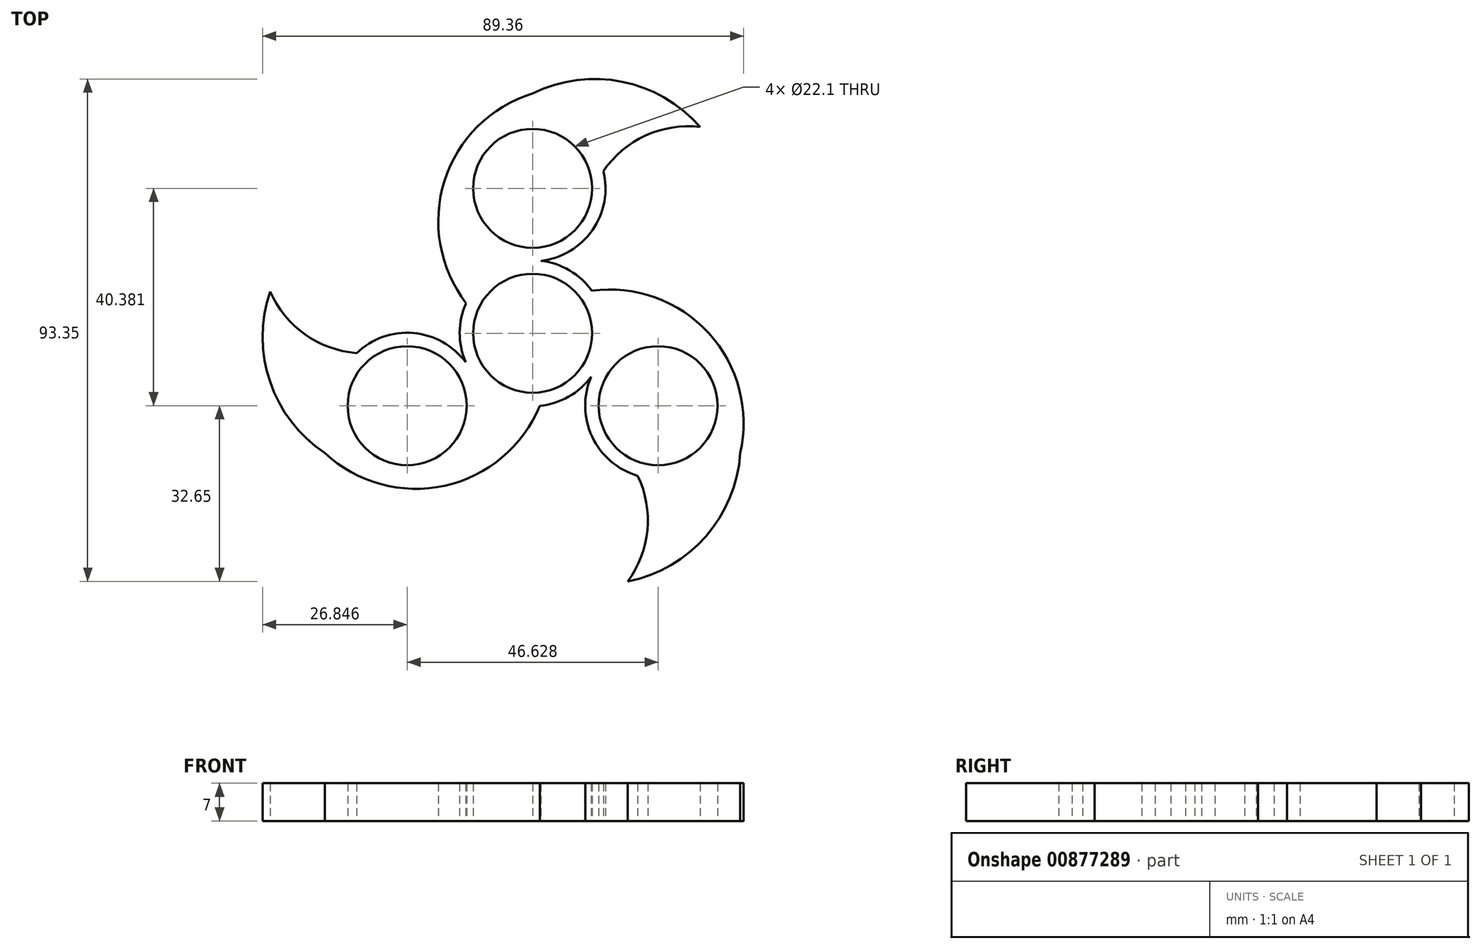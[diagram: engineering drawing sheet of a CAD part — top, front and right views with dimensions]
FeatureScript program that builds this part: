
annotation { "Feature Type Name" : "Feature", "Feature Type Description" : "" }
export const myFeature = defineFeature(function(context is Context, id is Id, definition is map)
    precondition{}
    {
        {
            var Q0;
            Q0=qCreatedBy(makeId("Top.planeOp"),FACE);
            var sketch = newSketch(context, id + "F0", { "sketchPlane" : qUnion([Q0])});
            skCircle(sketch, "E0", {"center": v(0, 0) * mm, "radius": 11.05 * mm});
            skCircle(sketch, "E1", {"center": v(0, 0) * mm, "radius": 13.55 * mm});
            skCircle(sketch, "E2", {"center": v(0, 26.92) * mm, "radius": 11.05 * mm});
            skCircle(sketch, "E3", {"center": v(0, 26.92) * mm, "radius": 13.55 * mm});
            skCircle(sketch, "E4.1.0", {"center": v(-23.31, -13.46) * mm, "radius": 11.05 * mm});
            skCircle(sketch, "E4.1.1", {"center": v(-23.31, -13.46) * mm, "radius": 13.55 * mm});
            skCircle(sketch, "E4.2.0", {"center": v(23.31, -13.46) * mm, "radius": 11.05 * mm});
            skCircle(sketch, "E4.2.1", {"center": v(23.31, -13.46) * mm, "radius": 13.55 * mm});
            skArc(sketch, "E5", {"start": v(31.1, 38.36) * mm, "mid": v(16.6, 46.74) * mm, "end": v(0, 44.54) * mm});
            skArc(sketch, "E6", {"start": v(31.1, 38.36) * mm, "mid": v(21, 36.74) * mm, "end": v(13.16, 30.14) * mm});
            skArc(sketch, "E7.1.0", {"start": v(-48.77, 7.75) * mm, "mid": v(-48.78, -9) * mm, "end": v(-38.58, -22.27) * mm});
            skArc(sketch, "E7.1.1", {"start": v(-48.77, 7.75) * mm, "mid": v(-42.3, -0.19) * mm, "end": v(-32.68, -3.67) * mm});
            skArc(sketch, "E7.2.0", {"start": v(17.67, -46.1) * mm, "mid": v(32.18, -37.75) * mm, "end": v(38.58, -22.27) * mm});
            skArc(sketch, "E7.2.1", {"start": v(17.67, -46.1) * mm, "mid": v(21.32, -36.55) * mm, "end": v(19.52, -26.47) * mm});
            skArc(sketch, "E8", {"start": v(0, 44.54) * mm, "mid": v(-16.37, 28.3) * mm, "end": v(-12.34, 5.6) * mm});
            skArc(sketch, "E9.1.0", {"start": v(-38.58, -22.27) * mm, "mid": v(-16.32, -28.33) * mm, "end": v(1.33, -13.48) * mm});
            skArc(sketch, "E9.2.0", {"start": v(38.58, -22.27) * mm, "mid": v(32.7, 0.03) * mm, "end": v(11.01, 7.9) * mm});
            skSolve(sketch);
        }
        {
            var Q0;
            {var subQ0=sQuery(id+"F0.wireOp",EDGE,"E1");var subQ1=sQuery(id+"F0.wireOp",EDGE,"E3");var subQ2=makeQuery(id+"F0.imprint","INTERSECT",VERTEX,{"disambiguationData":[OD(0.0)],"derivedFrom":[subQ1,subQ0]});Q0=makeQuery(id+"F0.imprint","IMPRINT",FACE,{"disambiguationData":[TD([[makeQuery(id+"F0.imprint","IMPRINT",EDGE,{"disambiguationData":[TD([[subQ2,1.0]])],"derivedFrom":subQ1}),1.0]])]});}
            var Q1;
            {var subQ0=sQuery(id+"F0.wireOp",EDGE,"E1");var subQ1=sQuery(id+"F0.wireOp",EDGE,"E4.1.1");var subQ2=makeQuery(id+"F0.imprint","INTERSECT",VERTEX,{"disambiguationData":[OD(0.0)],"derivedFrom":[subQ1,subQ0]});Q1=makeQuery(id+"F0.imprint","IMPRINT",FACE,{"disambiguationData":[TD([[makeQuery(id+"F0.imprint","IMPRINT",EDGE,{"disambiguationData":[TD([[subQ2,1.0]])],"derivedFrom":subQ1}),1.0]])]});}
            var Q2;
            {var subQ0=sQuery(id+"F0.wireOp",EDGE,"E1");var subQ1=sQuery(id+"F0.wireOp",EDGE,"E4.2.1");var subQ2=makeQuery(id+"F0.imprint","INTERSECT",VERTEX,{"disambiguationData":[OD(0.0)],"derivedFrom":[subQ1,subQ0]});Q2=makeQuery(id+"F0.imprint","IMPRINT",FACE,{"disambiguationData":[TD([[makeQuery(id+"F0.imprint","IMPRINT",EDGE,{"disambiguationData":[TD([[subQ2,1.0]])],"derivedFrom":subQ1}),1.0]])]});}
            var Q3;
            Q3=makeQuery(id+"F0.imprint","IMPRINT",FACE,{"disambiguationData":[TD([[makeQuery(id+"F0.imprint","IMPRINT",EDGE,{"derivedFrom":sQuery(id+"F0.wireOp",EDGE,"E2")}),-1.0]])]});
            var Q4;
            Q4=makeQuery(id+"F0.imprint","IMPRINT",FACE,{"disambiguationData":[TD([[makeQuery(id+"F0.imprint","IMPRINT",EDGE,{"derivedFrom":sQuery(id+"F0.wireOp",EDGE,"E4.1.0")}),-1.0]])]});
            var Q5;
            Q5=makeQuery(id+"F0.imprint","IMPRINT",FACE,{"disambiguationData":[TD([[makeQuery(id+"F0.imprint","IMPRINT",EDGE,{"derivedFrom":sQuery(id+"F0.wireOp",EDGE,"E4.2.0")}),-1.0]])]});
            var Q6;
            Q6=makeQuery(id+"F0.imprint","IMPRINT",FACE,{"disambiguationData":[TD([[makeQuery(id+"F0.imprint","IMPRINT",EDGE,{"derivedFrom":sQuery(id+"F0.wireOp",EDGE,"E0")}),-1.0]])]});
            var Q7;
            Q7=makeQuery(id+"F0.imprint","IMPRINT",FACE,{"disambiguationData":[TD([[makeQuery(id+"F0.imprint","IMPRINT",EDGE,{"derivedFrom":sQuery(id+"F0.wireOp",EDGE,"E7.1.0")}),1.0]])]});
            var Q8;
            Q8=makeQuery(id+"F0.imprint","IMPRINT",FACE,{"disambiguationData":[TD([[makeQuery(id+"F0.imprint","IMPRINT",EDGE,{"derivedFrom":sQuery(id+"F0.wireOp",EDGE,"E5")}),1.0]])]});
            var Q9;
            Q9=makeQuery(id+"F0.imprint","IMPRINT",FACE,{"disambiguationData":[TD([[makeQuery(id+"F0.imprint","IMPRINT",EDGE,{"derivedFrom":sQuery(id+"F0.wireOp",EDGE,"E7.2.0")}),1.0]])]});
            extrude(context, id + "F1", {"entities" : qUnion([Q0, Q1, Q2, Q3, Q4, Q5, Q6, Q7, Q8, Q9]), "depth" : 7 * mm, "offsetDistance" : 25 * mm});
        }
    });
